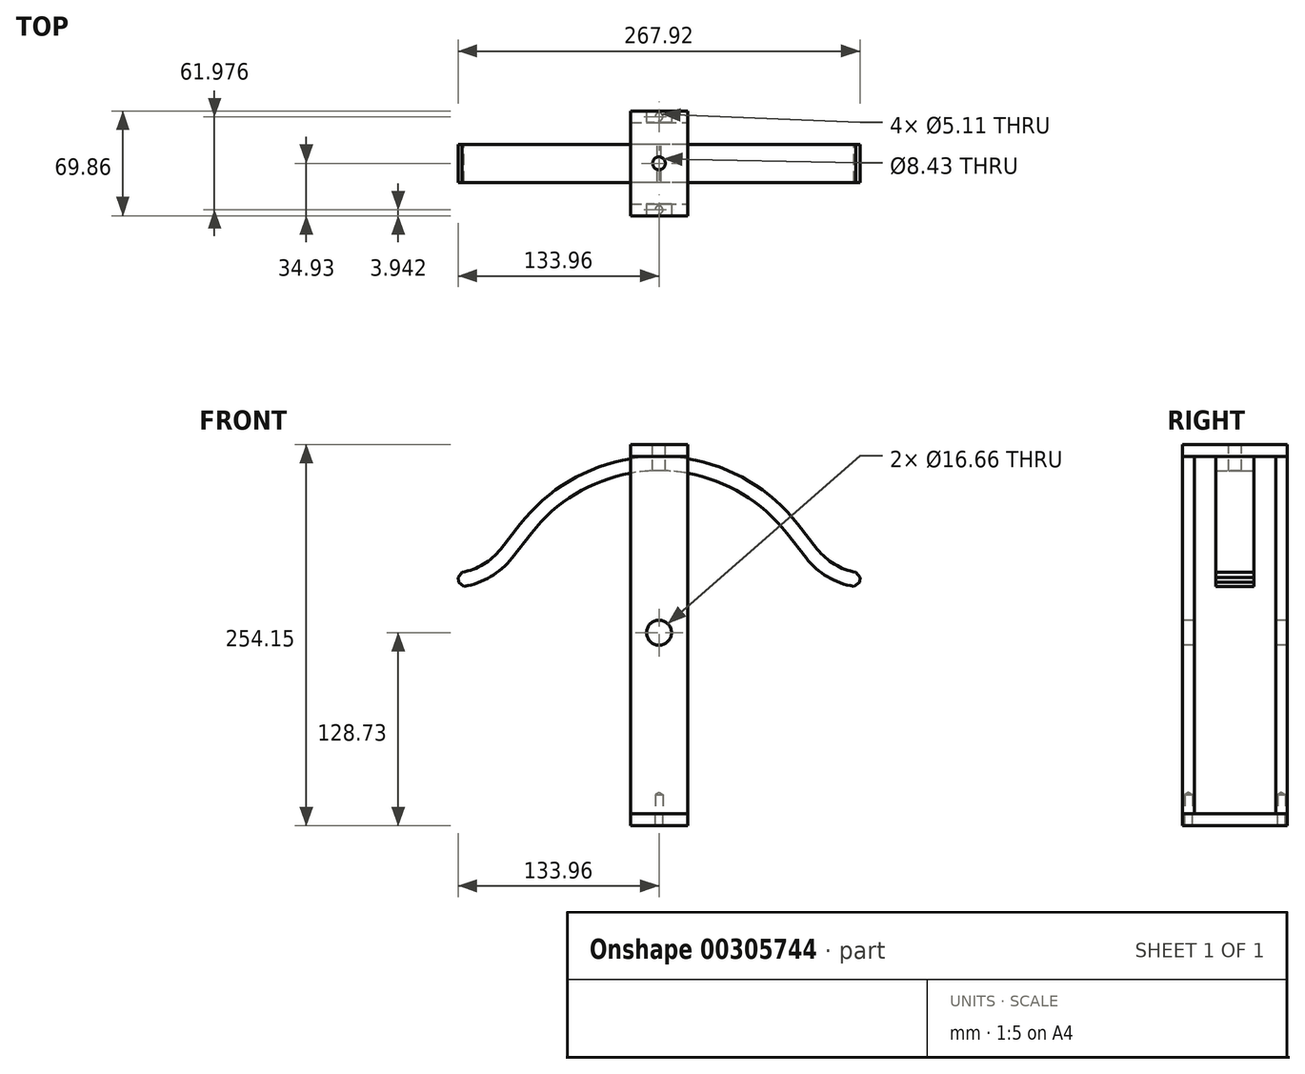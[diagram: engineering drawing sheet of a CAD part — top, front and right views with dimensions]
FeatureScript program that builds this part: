
annotation { "Feature Type Name" : "Feature", "Feature Type Description" : "" }
export const myFeature = defineFeature(function(context is Context, id is Id, definition is map)
    precondition{}
    {
        {
            var Q0;
            Q0=qCreatedBy(makeId("Front.planeOp"),FACE);
            var sketch = newSketch(context, id + "F0", { "sketchPlane" : qUnion([Q0])});
            skArc(sketch, "E0", {"start": v(-104.1, 28.57) * mm, "mid": v(0, -107.95) * mm, "end": v(104.1, 28.57) * mm});
            skArc(sketch, "E1.0", {"start": v(-113.95, 28.57) * mm, "mid": v(0, -117.48) * mm, "end": v(113.95, 28.58) * mm});
            skLineSegment(sketch, "E2", {"start": v(0, 140.03) * mm, "end": v(0, -149.62) * mm, "construction": true});
            skLineSegment(sketch, "E3", {"start": v(-208.33, 0) * mm, "end": v(172.38, 0) * mm, "construction": true});
            skLineSegment(sketch, "E4.0", {"start": v(-138.18, 140.03) * mm, "end": v(-138.18, -149.62) * mm, "construction": true});
            skLineSegment(sketch, "E5.0", {"start": v(-208.33, 28.58) * mm, "end": v(172.38, 28.58) * mm, "construction": true});
            skLineSegment(sketch, "E6.0", {"start": v(-208.33, 80.98) * mm, "end": v(172.38, 80.98) * mm, "construction": true});
            skArc(sketch, "E7", {"start": v(-133.35, 30.4) * mm, "mid": v(-113.75, 36.43) * mm, "end": v(-98.13, 49.72) * mm});
            skLineSegment(sketch, "E8", {"start": v(-85.1, 66.41) * mm, "end": v(-98.13, 49.72) * mm});
            skLineSegment(sketch, "E9.0", {"start": v(-133.35, 140.03) * mm, "end": v(-133.35, -149.62) * mm, "construction": true});
            skArc(sketch, "E10.trimOffspring", {"start": v(-87.44, 78.45) * mm, "mid": v(-87.4, 79.71) * mm, "end": v(-87.38, 80.98) * mm});
            skArc(sketch, "E11.0", {"start": v(-134.25, 39.89) * mm, "mid": v(-118.33, 44.79) * mm, "end": v(-105.64, 55.58) * mm});
            skLineSegment(sketch, "E11.1", {"start": v(-92.61, 72.27) * mm, "end": v(-105.64, 55.58) * mm});
            skLineSegment(sketch, "E12", {"start": v(-133.35, 30.4) * mm, "end": v(-134.25, 39.89) * mm});
            skLineSegment(sketch, "E13.MirrorCS", {"start": v(133.35, 30.4) * mm, "end": v(134.25, 39.89) * mm});
            skArc(sketch, "E14.MirrorCS", {"start": v(87.44, 78.45) * mm, "mid": v(87.4, 79.71) * mm, "end": v(87.38, 80.98) * mm});
            skLineSegment(sketch, "E15.MirrorCS", {"start": v(85.1, 66.41) * mm, "end": v(98.13, 49.72) * mm});
            skLineSegment(sketch, "E16.MirrorCS", {"start": v(92.61, 72.27) * mm, "end": v(105.64, 55.58) * mm});
            skArc(sketch, "E17.MirrorCS", {"start": v(134.25, 39.89) * mm, "mid": v(118.33, 44.79) * mm, "end": v(105.64, 55.58) * mm});
            skArc(sketch, "E18.MirrorCS", {"start": v(133.35, 30.4) * mm, "mid": v(113.75, 36.43) * mm, "end": v(98.13, 49.72) * mm});
            skArc(sketch, "E19.trimOffspring", {"start": v(92.61, 72.27) * mm, "mid": v(0, 117.48) * mm, "end": v(-92.61, 72.27) * mm});
            skArc(sketch, "E20.trimOffspring", {"start": v(85.1, 66.41) * mm, "mid": v(0, 107.95) * mm, "end": v(-85.1, 66.41) * mm});
            skSolve(sketch);
        }
        {
            var Q0;
            Q0 = qSketchRegion(id + "F0", true);
            extrude(context, id + "F1", {"entities" : qUnion([Q0]), "endBound" : BoundingType.SYMMETRIC, "depth" : 25.4 * mm});
        }
        {
            var Q0;
            Q0=makeQuery(id+"F1.opExtrude","SWEPT_EDGE",EDGE,{"disambiguationData":[OSD([sQuery(id+"F0.wireOp",EDGE,"E13.MirrorCS"),sQuery(id+"F0.wireOp",EDGE,"E17.MirrorCS")])]});
            var Q1;
            Q1=makeQuery(id+"F1.opExtrude","SWEPT_EDGE",EDGE,{"disambiguationData":[OSD([sQuery(id+"F0.wireOp",EDGE,"E13.MirrorCS"),sQuery(id+"F0.wireOp",EDGE,"E18.MirrorCS")])]});
            var Q2;
            Q2=makeQuery(id+"F1.opExtrude","SWEPT_EDGE",EDGE,{"disambiguationData":[OSD([sQuery(id+"F0.wireOp",EDGE,"E11.0"),sQuery(id+"F0.wireOp",EDGE,"E12")])]});
            var Q3;
            Q3=makeQuery(id+"F1.opExtrude","SWEPT_EDGE",EDGE,{"disambiguationData":[OSD([sQuery(id+"F0.wireOp",EDGE,"E7"),sQuery(id+"F0.wireOp",EDGE,"E12")])]});
            chamfer(context, id + "F2", {"entities" : qUnion([Q0, Q1, Q2, Q3]), "width" : 3.17 * mm, "tangentPropagation" : true});
        }
        {
            var Q0;
            Q0=qCreatedBy(makeId("Front.planeOp"),FACE);
            var sketch = newSketch(context, id + "F3", { "sketchPlane" : qUnion([Q0])});
            skLineSegment(sketch, "E21", {"start": v(0, -36.18) * mm, "end": v(0, 0) * mm, "construction": true});
            skArc(sketch, "E22.0", {"start": v(92.61, 72.27) * mm, "mid": v(0, 117.48) * mm, "end": v(-92.61, 72.27) * mm, "construction": true});
            skLineSegment(sketch, "E23.trimOffspring", {"start": v(0, 117.47) * mm, "end": v(0, 151.71) * mm, "construction": true});
            skLineSegment(sketch, "E24", {"start": v(0, 117.47) * mm, "end": v(-56.03, 117.47) * mm, "construction": true});
            skLineSegment(sketch, "E25.0", {"start": v(0, 121.44) * mm, "end": v(-56.03, 121.44) * mm, "construction": true});
            skLineSegment(sketch, "E26.bottom", {"start": v(-19.05, 117.47) * mm, "end": v(19.05, 117.47) * mm});
            skLineSegment(sketch, "E26.top", {"start": v(-19.05, 125.42) * mm, "end": v(19.05, 125.42) * mm});
            skLineSegment(sketch, "E26.left", {"start": v(-19.05, 117.47) * mm, "end": v(-19.05, 125.42) * mm});
            skLineSegment(sketch, "E26.right", {"start": v(19.05, 117.47) * mm, "end": v(19.05, 125.42) * mm});
            skPoint(sketch, "E26.middle", {"position": v(0, 121.44) * mm});
            skSolve(sketch);
        }
        {
            var Q0;
            Q0 = qSketchRegion(id + "F3", true);
            extrude(context, id + "F4", {"entities" : qUnion([Q0]), "operationType" : NewBodyOperationType.ADD, "endBound" : BoundingType.SYMMETRIC, "depth" : 69.85 * mm});
        }
        {
            var Q0;
            Q0=makeQuery(id+"F4.opExtrude","SWEPT_FACE",FACE,{"disambiguationData":[OSD([sQuery(id+"F3.wireOp",EDGE,"E26.bottom")])]});
            var sketch = newSketch(context, id + "F5", { "sketchPlane" : qUnion([Q0])});
            skLineSegment(sketch, "E27.bottom", {"start": v(-19.05, 34.93) * mm, "end": v(19.05, 34.93) * mm});
            skLineSegment(sketch, "E27.top", {"start": v(-19.05, 27.05) * mm, "end": v(19.05, 27.05) * mm});
            skLineSegment(sketch, "E27.left", {"start": v(-19.05, 34.93) * mm, "end": v(-19.05, 27.05) * mm});
            skLineSegment(sketch, "E27.right", {"start": v(19.05, 34.93) * mm, "end": v(19.05, 27.05) * mm});
            skLineSegment(sketch, "E28", {"start": v(-162.59, 0) * mm, "end": v(157.82, 0) * mm, "construction": true});
            skLineSegment(sketch, "E29.MirrorCS", {"start": v(-19.05, -34.93) * mm, "end": v(-19.05, -27.05) * mm});
            skLineSegment(sketch, "E30.MirrorCS", {"start": v(19.05, -34.93) * mm, "end": v(19.05, -27.05) * mm});
            skLineSegment(sketch, "E31.MirrorCS", {"start": v(-19.05, -34.93) * mm, "end": v(19.05, -34.93) * mm});
            skLineSegment(sketch, "E32.MirrorCS", {"start": v(-19.05, -27.05) * mm, "end": v(19.05, -27.05) * mm});
            skSolve(sketch);
        }
        {
            var Q0;
            Q0 = qSketchRegion(id + "F5", true);
            extrude(context, id + "F6", {"entities" : qUnion([Q0]), "depth" : 238.25 * mm});
        }
        {
            var Q0;
            Q0=makeQuery(id+"F6.boolean.opBoolean","MERGE",FACE,{"derivedFrom":[makeQuery(id+"F4.opExtrude","CAP_FACE",FACE,{"disambiguationData":[OSD([sQuery(id+"F3.wireOp",EDGE,"E26.bottom"),sQuery(id+"F3.wireOp",EDGE,"E26.top"),sQuery(id+"F3.wireOp",EDGE,"E26.left"),sQuery(id+"F3.wireOp",EDGE,"E26.right")])],"isStart":false}),makeQuery(id+"F6.opExtrude","SWEPT_FACE",FACE,{"disambiguationData":[OSD([sQuery(id+"F5.wireOp",EDGE,"E27.bottom")])]})]});
            var sketch = newSketch(context, id + "F7", { "sketchPlane" : qUnion([Q0])});
            skLineSegment(sketch, "E33.0", {"start": v(-19.05, 125.42) * mm, "end": v(19.05, 125.42) * mm, "construction": true});
            skLineSegment(sketch, "E34", {"start": v(0, 125.42) * mm, "end": v(0, -0.06) * mm, "construction": true});
            skPoint(sketch, "E34.endSnap0", {"position": v(0, 125.42) * mm});
            skPoint(sketch, "E35", {"position": v(0, 0) * mm});
            skSolve(sketch);
        }
        {
            var Q0;
            Q0=sQuery(id+"F7.wireOp",VERTEX,"E35");
            var Q1;
            Q1=makeQuery(id+"F6.opExtrude","SWEPT_BODY",BODY,{"disambiguationData":[OSD([sQuery(id+"F5.wireOp",EDGE,"E29.MirrorCS"),sQuery(id+"F5.wireOp",EDGE,"E30.MirrorCS"),sQuery(id+"F5.wireOp",EDGE,"E31.MirrorCS"),sQuery(id+"F5.wireOp",EDGE,"E32.MirrorCS")])]});
            var Q2;
            Q2=makeQuery(id+"F6.opExtrude","SWEPT_BODY",BODY,{"disambiguationData":[OSD([sQuery(id+"F5.wireOp",EDGE,"E27.bottom"),sQuery(id+"F5.wireOp",EDGE,"E27.top"),sQuery(id+"F5.wireOp",EDGE,"E27.left"),sQuery(id+"F5.wireOp",EDGE,"E27.right")])]});
            hole(context, id + "F8", {"style" : HoleStyle.SIMPLE, "endStyle" : HoleEndStyle.THROUGH, "holeDiameter" : 16.66 * mm, "tappedDepth" : 24.13 * mm, "tapClearance" : 3, "startFromSketch" : true, "locations" : qUnion([Q0]), "scope" : qUnion([Q1, Q2])});
        }
        {
            var Q0;
            Q0=makeQuery(id+"F6.opExtrude","CAP_FACE",FACE,{"disambiguationData":[OSD([sQuery(id+"F5.wireOp",EDGE,"E27.bottom"),sQuery(id+"F5.wireOp",EDGE,"E27.top"),sQuery(id+"F5.wireOp",EDGE,"E27.left"),sQuery(id+"F5.wireOp",EDGE,"E27.right")])],"isStart":false});
            var sketch = newSketch(context, id + "F9", { "sketchPlane" : qUnion([Q0])});
            skLineSegment(sketch, "E36", {"start": v(0, 34.93) * mm, "end": v(0, -34.89) * mm, "construction": true});
            skLineSegment(sketch, "E37", {"start": v(-19.05, 30.99) * mm, "end": v(6.98, 30.99) * mm, "construction": true});
            skLineSegment(sketch, "E38.0", {"start": v(19.05, -27.05) * mm, "end": v(19.05, -34.93) * mm, "construction": true});
            skLineSegment(sketch, "E39", {"start": v(19.05, -30.99) * mm, "end": v(-5.8, -30.99) * mm, "construction": true});
            skPoint(sketch, "E40", {"position": v(0, 30.99) * mm});
            skPoint(sketch, "E41", {"position": v(0, -30.99) * mm});
            skSolve(sketch);
        }
        {
            var Q0;
            Q0=sQuery(id+"F9.wireOp",VERTEX,"E40");
            var Q1;
            Q1=sQuery(id+"F9.wireOp",VERTEX,"E41");
            var Q2;
            Q2=makeQuery(id+"F1.opExtrude","SWEPT_BODY",BODY,{"disambiguationData":[OSD([sQuery(id+"F0.wireOp",EDGE,"E7"),sQuery(id+"F0.wireOp",EDGE,"E8"),sQuery(id+"F0.wireOp",EDGE,"E11.0"),sQuery(id+"F0.wireOp",EDGE,"E11.1"),sQuery(id+"F0.wireOp",EDGE,"E12"),sQuery(id+"F0.wireOp",EDGE,"E13.MirrorCS"),sQuery(id+"F0.wireOp",EDGE,"E15.MirrorCS"),sQuery(id+"F0.wireOp",EDGE,"E16.MirrorCS"),sQuery(id+"F0.wireOp",EDGE,"E17.MirrorCS"),sQuery(id+"F0.wireOp",EDGE,"E18.MirrorCS"),sQuery(id+"F0.wireOp",EDGE,"E19.trimOffspring"),sQuery(id+"F0.wireOp",EDGE,"E20.trimOffspring")])]});
            var Q3;
            Q3=makeQuery(id+"F6.opExtrude","SWEPT_BODY",BODY,{"disambiguationData":[OSD([sQuery(id+"F5.wireOp",EDGE,"E27.bottom"),sQuery(id+"F5.wireOp",EDGE,"E27.top"),sQuery(id+"F5.wireOp",EDGE,"E27.left"),sQuery(id+"F5.wireOp",EDGE,"E27.right")])]});
            var Q4;
            Q4=makeQuery(id+"F6.opExtrude","SWEPT_BODY",BODY,{"disambiguationData":[OSD([sQuery(id+"F5.wireOp",EDGE,"E29.MirrorCS"),sQuery(id+"F5.wireOp",EDGE,"E30.MirrorCS"),sQuery(id+"F5.wireOp",EDGE,"E31.MirrorCS"),sQuery(id+"F5.wireOp",EDGE,"E32.MirrorCS")])]});
            hole(context, id + "F10", {"style" : HoleStyle.SIMPLE, "endStyle" : HoleEndStyle.BLIND, "standardTappedOrClearance" : lookupTablePath({ "standard" : "ANSI", "fit" : "Normal (ASME)", "size" : "#10", "type" : "Clearance" }), "standardBlindInLast" : lookupTablePath({ "fit" : "Free", "standard" : "ANSI", "size" : "#10", "type" : "Clearance" }), "holeDiameter" : 5.1 * mm, "holeDepth" : 12.7 * mm, "tappedDepth" : 24.13 * mm, "tapClearance" : 3, "startFromSketch" : true, "locations" : qUnion([Q0, Q1]), "scope" : qUnion([Q2, Q3, Q4])});
        }
        {
            var Q0;
            Q0=makeQuery(id+"F4.opExtrude","SWEPT_FACE",FACE,{"disambiguationData":[OSD([sQuery(id+"F3.wireOp",EDGE,"E26.top")])]});
            var sketch = newSketch(context, id + "F11", { "sketchPlane" : qUnion([Q0])});
            skLineSegment(sketch, "E42.0.0", {"start": v(19.05, 34.93) * mm, "end": v(-19.05, 34.93) * mm, "construction": true});
            skLineSegment(sketch, "E42.0.1", {"start": v(-19.05, 34.93) * mm, "end": v(-19.05, -34.93) * mm, "construction": true});
            skLineSegment(sketch, "E42.0.2", {"start": v(-19.05, -34.93) * mm, "end": v(19.05, -34.93) * mm, "construction": true});
            skLineSegment(sketch, "E42.0.3", {"start": v(19.05, -34.93) * mm, "end": v(19.05, 34.93) * mm, "construction": true});
            skLineSegment(sketch, "E43", {"start": v(0, 34.93) * mm, "end": v(0, -34.93) * mm, "construction": true});
            skPoint(sketch, "E44", {"position": v(0, 0) * mm});
            skSolve(sketch);
        }
        {
            var Q0;
            Q0=sQuery(id+"F11.wireOp",VERTEX,"E44");
            var Q1;
            Q1=makeQuery(id+"F1.opExtrude","SWEPT_BODY",BODY,{"disambiguationData":[OSD([sQuery(id+"F0.wireOp",EDGE,"E7"),sQuery(id+"F0.wireOp",EDGE,"E8"),sQuery(id+"F0.wireOp",EDGE,"E11.0"),sQuery(id+"F0.wireOp",EDGE,"E11.1"),sQuery(id+"F0.wireOp",EDGE,"E12"),sQuery(id+"F0.wireOp",EDGE,"E13.MirrorCS"),sQuery(id+"F0.wireOp",EDGE,"E15.MirrorCS"),sQuery(id+"F0.wireOp",EDGE,"E16.MirrorCS"),sQuery(id+"F0.wireOp",EDGE,"E17.MirrorCS"),sQuery(id+"F0.wireOp",EDGE,"E18.MirrorCS"),sQuery(id+"F0.wireOp",EDGE,"E19.trimOffspring"),sQuery(id+"F0.wireOp",EDGE,"E20.trimOffspring")])]});
            hole(context, id + "F12", {"style" : HoleStyle.SIMPLE, "endStyle" : HoleEndStyle.BLIND, "standardTappedOrClearance" : lookupTablePath({ "standard" : "ANSI", "engagement" : "75%", "pitch" : "24 tpi", "size" : "3/8", "type" : "Tapped" }), "standardBlindInLast" : lookupTablePath({ "standard" : "ANSI", "engagement" : "75%", "pitch" : "24 tpi", "size" : "3/8", "type" : "Tapped" }), "holeDiameter" : 8.43 * mm, "showTappedDepth" : true, "holeDepth" : 27.3 * mm, "tappedDepth" : 24.13 * mm, "tapClearance" : 3, "startFromSketch" : true, "locations" : qUnion([Q0]), "scope" : qUnion([Q1]), "majorDiameter" : 9.53 * mm});
        }
        {
            var Q0;
            Q0=makeQuery(id+"F6.opExtrude","CAP_FACE",FACE,{"disambiguationData":[OSD([sQuery(id+"F5.wireOp",EDGE,"E29.MirrorCS"),sQuery(id+"F5.wireOp",EDGE,"E30.MirrorCS"),sQuery(id+"F5.wireOp",EDGE,"E31.MirrorCS"),sQuery(id+"F5.wireOp",EDGE,"E32.MirrorCS")])],"isStart":false});
            var sketch = newSketch(context, id + "F13", { "sketchPlane" : qUnion([Q0])});
            skLineSegment(sketch, "E45.0", {"start": v(-19.05, 34.93) * mm, "end": v(19.05, 34.93) * mm, "construction": true});
            skLineSegment(sketch, "E46.0", {"start": v(-19.05, -34.93) * mm, "end": v(19.05, -34.93) * mm, "construction": true});
            skLineSegment(sketch, "E47.bottom", {"start": v(-19.05, -34.93) * mm, "end": v(19.05, -34.93) * mm});
            skLineSegment(sketch, "E47.top", {"start": v(-19.05, 34.93) * mm, "end": v(19.05, 34.93) * mm});
            skLineSegment(sketch, "E47.left", {"start": v(-19.05, -34.93) * mm, "end": v(-19.05, 34.93) * mm});
            skLineSegment(sketch, "E47.right", {"start": v(19.05, -34.93) * mm, "end": v(19.05, 34.93) * mm});
            skCircle(sketch, "E48.0", {"center": v(0, -30.99) * mm, "radius": 2.55 * mm});
            skCircle(sketch, "E49.0", {"center": v(0, 30.99) * mm, "radius": 2.55 * mm});
            skSolve(sketch);
        }
        {
            var Q0;
            Q0 = qSketchRegion(id + "F13", true);
            extrude(context, id + "F14", {"entities" : qUnion([Q0]), "depth" : 7.95 * mm});
        }
    });
